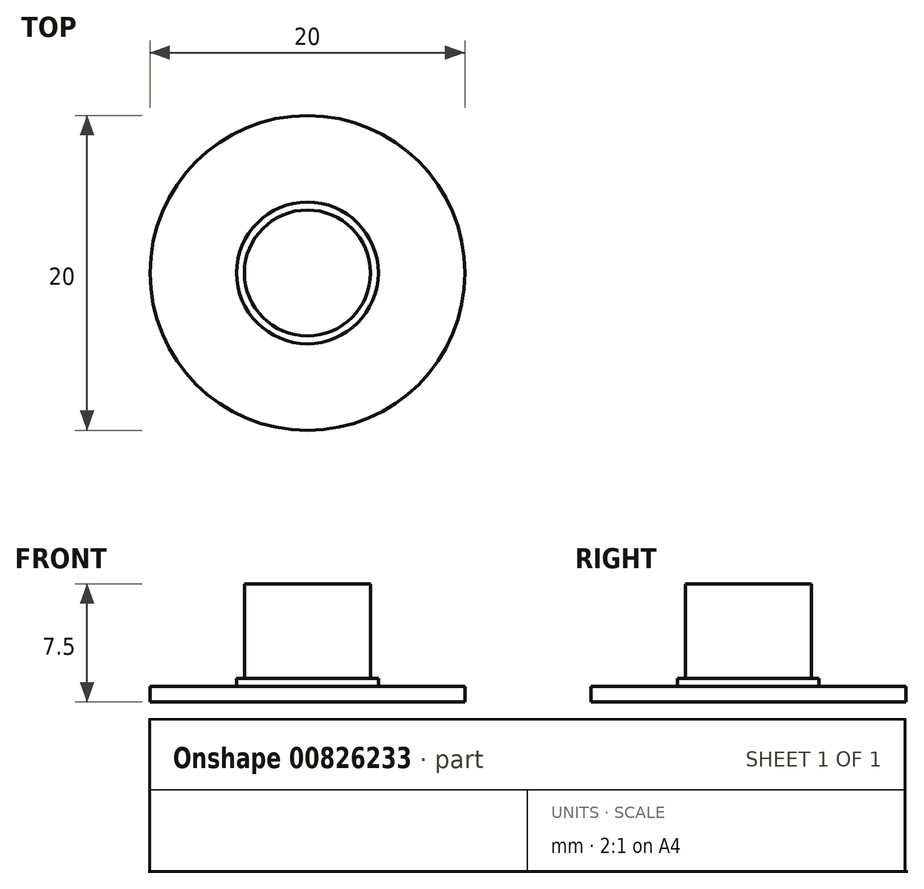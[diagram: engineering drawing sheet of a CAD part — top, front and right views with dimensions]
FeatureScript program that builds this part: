
annotation { "Feature Type Name" : "Feature", "Feature Type Description" : "" }
export const myFeature = defineFeature(function(context is Context, id is Id, definition is map)
    precondition{}
    {
        {
            var Q0;
            Q0=qCreatedBy(makeId("Top.planeOp"),FACE);
            var sketch = newSketch(context, id + "F0", { "sketchPlane" : qUnion([Q0])});
            skCircle(sketch, "E0", {"center": v(0, 0) * mm, "radius": 10 * mm});
            skSolve(sketch);
        }
        {
            var Q0;
            Q0=qSketchRegion(id+"F0",true);
            extrude(context, id + "F1", {"entities" : qUnion([Q0]), "depth" : 1 * mm, "offsetDistance" : 25 * mm});
        }
        {
            var Q0;
            Q0=makeQuery(id+"F1.opExtrude","CAP_FACE",FACE,{"disambiguationData":[OSD([sQuery(id+"F0.wireOp",EDGE,"E0")])],"isStart":false});
            var sketch = newSketch(context, id + "F2", { "sketchPlane" : qUnion([Q0])});
            skCircle(sketch, "E1", {"center": v(0, 0) * mm, "radius": 4.5 * mm});
            skSolve(sketch);
        }
        {
            var Q0;
            Q0=makeQuery(id+"F2.imprint","IMPRINT",FACE,{"disambiguationData":[TD([[makeQuery(id+"F2.imprint","IMPRINT",EDGE,{"derivedFrom":sQuery(id+"F2.wireOp",EDGE,"E1")}),1.0]])]});
            extrude(context, id + "F3", {"entities" : qUnion([Q0]), "operationType" : NewBodyOperationType.ADD, "depth" : .5 * mm, "offsetDistance" : 25 * mm});
        }
        {
            var Q0;
            Q0=makeQuery(id+"F3.opExtrude","CAP_FACE",FACE,{"disambiguationData":[OSD([sQuery(id+"F2.wireOp",EDGE,"E1")])],"isStart":false});
            var sketch = newSketch(context, id + "F4", { "sketchPlane" : qUnion([Q0])});
            skCircle(sketch, "E2", {"center": v(0, 0) * mm, "radius": 4 * mm});
            skSolve(sketch);
        }
        {
            var Q0;
            Q0=makeQuery(id+"F4.imprint","IMPRINT",FACE,{"disambiguationData":[TD([[makeQuery(id+"F4.imprint","IMPRINT",EDGE,{"derivedFrom":sQuery(id+"F4.wireOp",EDGE,"E2")}),1.0]])]});
            extrude(context, id + "F5", {"entities" : qUnion([Q0]), "operationType" : NewBodyOperationType.ADD, "depth" : 6 * mm, "offsetDistance" : 25 * mm});
        }
    });
